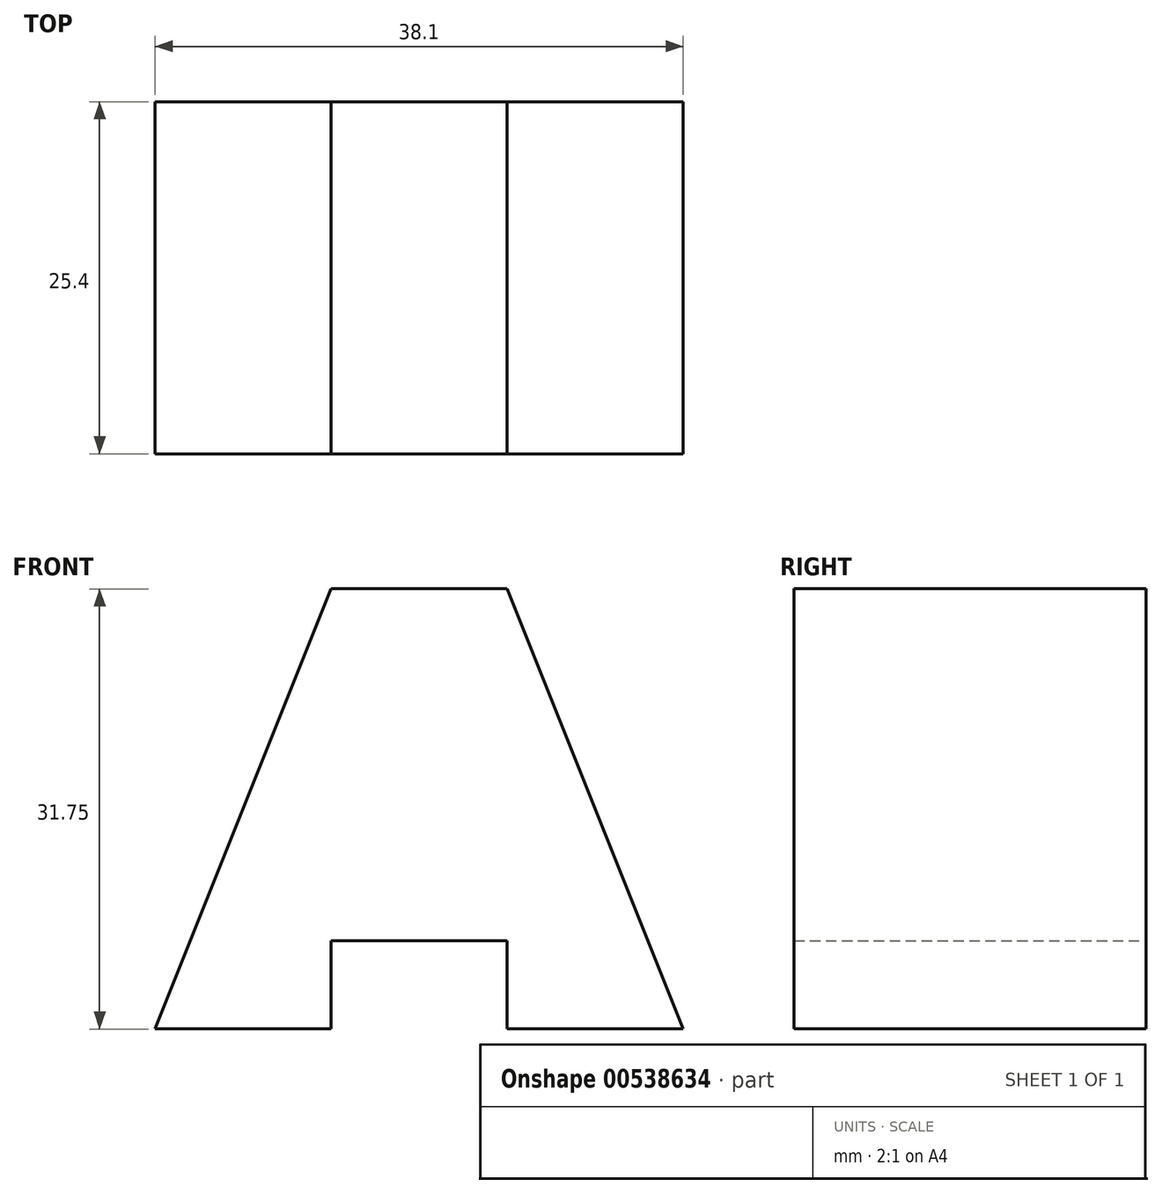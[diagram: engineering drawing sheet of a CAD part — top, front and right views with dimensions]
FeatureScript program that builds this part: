
annotation { "Feature Type Name" : "Feature", "Feature Type Description" : "" }
export const myFeature = defineFeature(function(context is Context, id is Id, definition is map)
    precondition{}
    {
        {
            var Q0;
            Q0=qCreatedBy(makeId("Front.planeOp"),FACE);
            var sketch = newSketch(context, id + "F0", { "sketchPlane" : qUnion([Q0])});
            skLineSegment(sketch, "E0", {"start": v(-53.74, 38.16) * mm, "end": v(-41.04, 38.16) * mm});
            skLineSegment(sketch, "E1", {"start": v(-41.04, 12.76) * mm, "end": v(-53.74, 12.76) * mm});
            skLineSegment(sketch, "E2", {"start": v(-28.34, 6.41) * mm, "end": v(-41.04, 6.41) * mm});
            skLineSegment(sketch, "E3", {"start": v(-41.04, 6.41) * mm, "end": v(-41.04, 12.76) * mm});
            skLineSegment(sketch, "E4", {"start": v(-53.74, 12.76) * mm, "end": v(-53.74, 6.41) * mm});
            skLineSegment(sketch, "E5", {"start": v(-53.74, 6.41) * mm, "end": v(-66.44, 6.41) * mm});
            skLineSegment(sketch, "E6", {"start": v(-66.44, 6.41) * mm, "end": v(-53.74, 38.16) * mm});
            skLineSegment(sketch, "E7", {"start": v(-41.04, 38.16) * mm, "end": v(-28.34, 6.41) * mm});
            skSolve(sketch);
        }
        {
            var Q0;
            Q0=makeQuery(id+"F0.imprint","IMPRINT",FACE,{"disambiguationData":[TD([[makeQuery(id+"F0.imprint","IMPRINT",EDGE,{"derivedFrom":sQuery(id+"F0.wireOp",EDGE,"E0")}),-1.0]])]});
            extrude(context, id + "F1", {"entities" : qUnion([Q0]), "depth" : 25.4 * mm, "offsetDistance" : 25.4 * mm});
        }
    });
